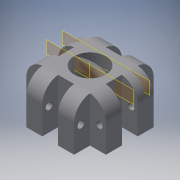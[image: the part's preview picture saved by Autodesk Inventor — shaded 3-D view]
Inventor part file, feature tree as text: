
AUTODESK INVENTOR PART (.ipt)
format: ipt  version: 2018 (Build 220112000, 112)  size: 298,496 bytes
history: native  units: mm
features: sketch x4, extrude x3, plane x2, fillet x2, pattern_circular x1, other x1, helix x1
ambient origin geometry x8: Origin, YZ Plane, XZ Plane, XY Plane, X Axis, Y Axis, Z Axis, Center Point
bodies: Solid1 (feature_tree)
feature tree (14):
  extrude  "Extrusion1"  Depth=20.0mm
  extrude  "Extrusion6"  Depth=7.0mm
  extrude  "Extrusion7"  Depth=7.0mm
  pattern_circular  "Circular Pattern3"  [2 undecoded]
  plane  "Work Plane3"
  sketch  "Sketch10"  dims[d59=7.0mm d60=7.0mm d61=7.0mm d62=90.0deg d63=7.0mm d64=7.0mm d65=90.0deg d66=7.0mm d67=7.0mm d68=7.0mm d69=7.0mm d70=7.0mm d71=7.0mm d72=7.0mm d73=7.0mm d74=7.0mm d75=7.0mm d76=7.0mm d77=90.0deg d78=13.0mm d81=10.0mm d82=0.0mm d83=3.0mm d84=3.0mm d85=10.0mm d86=0.0mm d87=40.0mm d88=360.0deg d93=7.0mm d94=14.0mm d95=7.0mm d100=2.5mm d101=5.0mm d102=25.0mm d103=15.0mm d104=10.0mm d105=0.0mm d106=90.0deg d107=90.0deg d108=0.0mm d109=0.0mm d111=2.0mm d112=8.0mm]
  other  "Work Axis1"
  helix  "Coil1"  [1 undecoded]
  fillet  "Fillet4"  [1 undecoded]
  fillet  "Fillet5"  Radius=7.0mm
  sketch  "Sketch1"  dims[d28=20.0mm d29=0.0mm d49=13.0mm]
  sketch  "Sketch6"  dims[d55=7.0mm d56=7.0mm]
  sketch  "Sketch7"  dims[d57=7.0mm d58=7.0mm]
  plane  "Work Plane2"
note: 4 required parameter values undecoded (feature->parameter linkage not recoverable at this tier; creation-order binding heuristic only, values carry confidence <= 0.55)
